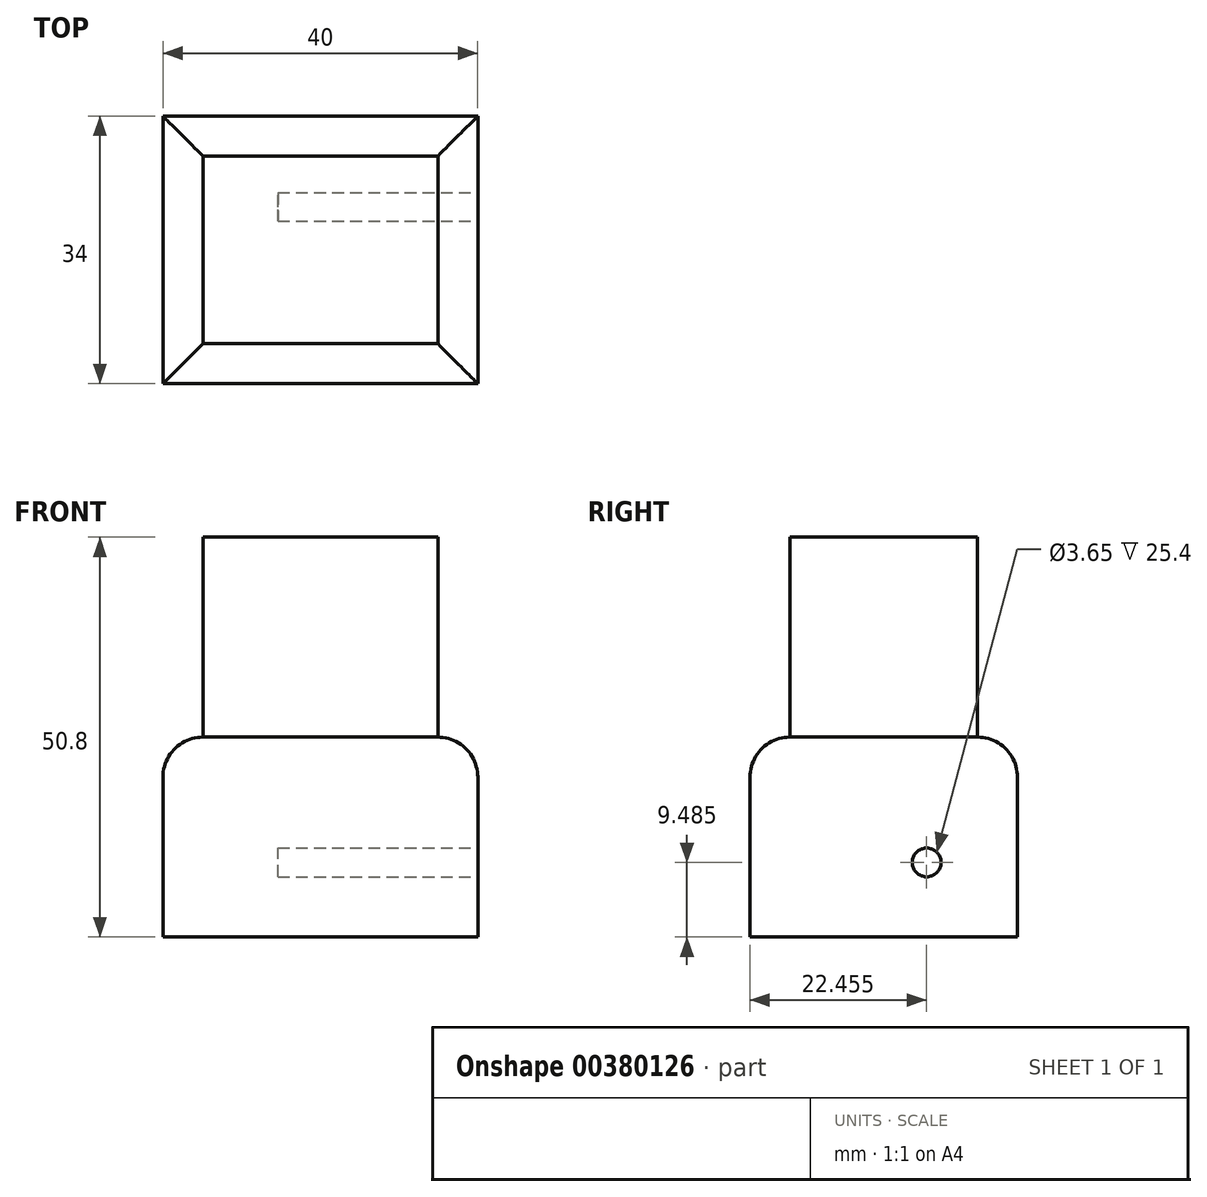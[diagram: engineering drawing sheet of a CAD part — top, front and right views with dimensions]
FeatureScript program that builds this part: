
annotation { "Feature Type Name" : "Feature", "Feature Type Description" : "" }
export const myFeature = defineFeature(function(context is Context, id is Id, definition is map)
    precondition{}
    {
        {
            var Q0;
            Q0=qCreatedBy(makeId("Top.planeOp"),FACE);
            var sketch = newSketch(context, id + "F0", { "sketchPlane" : qUnion([Q0])});
            skLineSegment(sketch, "E0.bottom", {"start": v(-57.95, 75.42) * mm, "end": v(-17.95, 75.42) * mm});
            skLineSegment(sketch, "E0.top", {"start": v(-57.95, 41.42) * mm, "end": v(-17.95, 41.42) * mm});
            skLineSegment(sketch, "E0.left", {"start": v(-57.95, 75.42) * mm, "end": v(-57.95, 41.42) * mm});
            skLineSegment(sketch, "E0.right", {"start": v(-17.95, 75.42) * mm, "end": v(-17.95, 41.42) * mm});
            skSolve(sketch);
        }
        {
            var Q0;
            Q0=makeQuery(id+"F0.imprint","IMPRINT",FACE,{"disambiguationData":[TD([[makeQuery(id+"F0.imprint","IMPRINT",EDGE,{"derivedFrom":sQuery(id+"F0.wireOp",EDGE,"E0.bottom")}),-1.0]])]});
            extrude(context, id + "F1", {"entities" : qUnion([Q0]), "depth" : 25.4 * mm});
        }
        {
            var Q0;
            Q0=makeQuery(id+"F1.opExtrude","SWEPT_FACE",FACE,{"disambiguationData":[OSD([sQuery(id+"F0.wireOp",EDGE,"E0.right")])]});
            var sketch = newSketch(context, id + "F2", { "sketchPlane" : qUnion([Q0])});
            skCircle(sketch, "E1", {"center": v(63.87, 9.48) * mm, "radius": 1.83 * mm});
            skSolve(sketch);
        }
        {
            var Q0;
            Q0 = qSketchRegion(id + "F2", true);
            extrude(context, id + "F3", {"entities" : qUnion([Q0]), "operationType" : NewBodyOperationType.REMOVE, "oppositeDirection" : true, "depth" : 25.4 * mm});
        }
        {
            var Q0;
            Q0=makeQuery(id+"F1.opExtrude","CAP_FACE",FACE,{"disambiguationData":[OSD([sQuery(id+"F0.wireOp",EDGE,"E0.bottom"),sQuery(id+"F0.wireOp",EDGE,"E0.top"),sQuery(id+"F0.wireOp",EDGE,"E0.left"),sQuery(id+"F0.wireOp",EDGE,"E0.right")])],"isStart":false});
            fillet(context, id + "F4", {"entities" : qUnion([Q0]), "radius" : 5.08 * mm, "tangentPropagation" : true, "allowEdgeOverflow" : false});
        }
        {
            var Q0;
            Q0=makeQuery(id+"F1.opExtrude","CAP_FACE",FACE,{"disambiguationData":[OSD([sQuery(id+"F0.wireOp",EDGE,"E0.bottom"),sQuery(id+"F0.wireOp",EDGE,"E0.top"),sQuery(id+"F0.wireOp",EDGE,"E0.left"),sQuery(id+"F0.wireOp",EDGE,"E0.right")])],"isStart":false});
            extrude(context, id + "F5", {"entities" : qUnion([Q0]), "operationType" : NewBodyOperationType.ADD, "depth" : 25.4 * mm});
        }
    });
